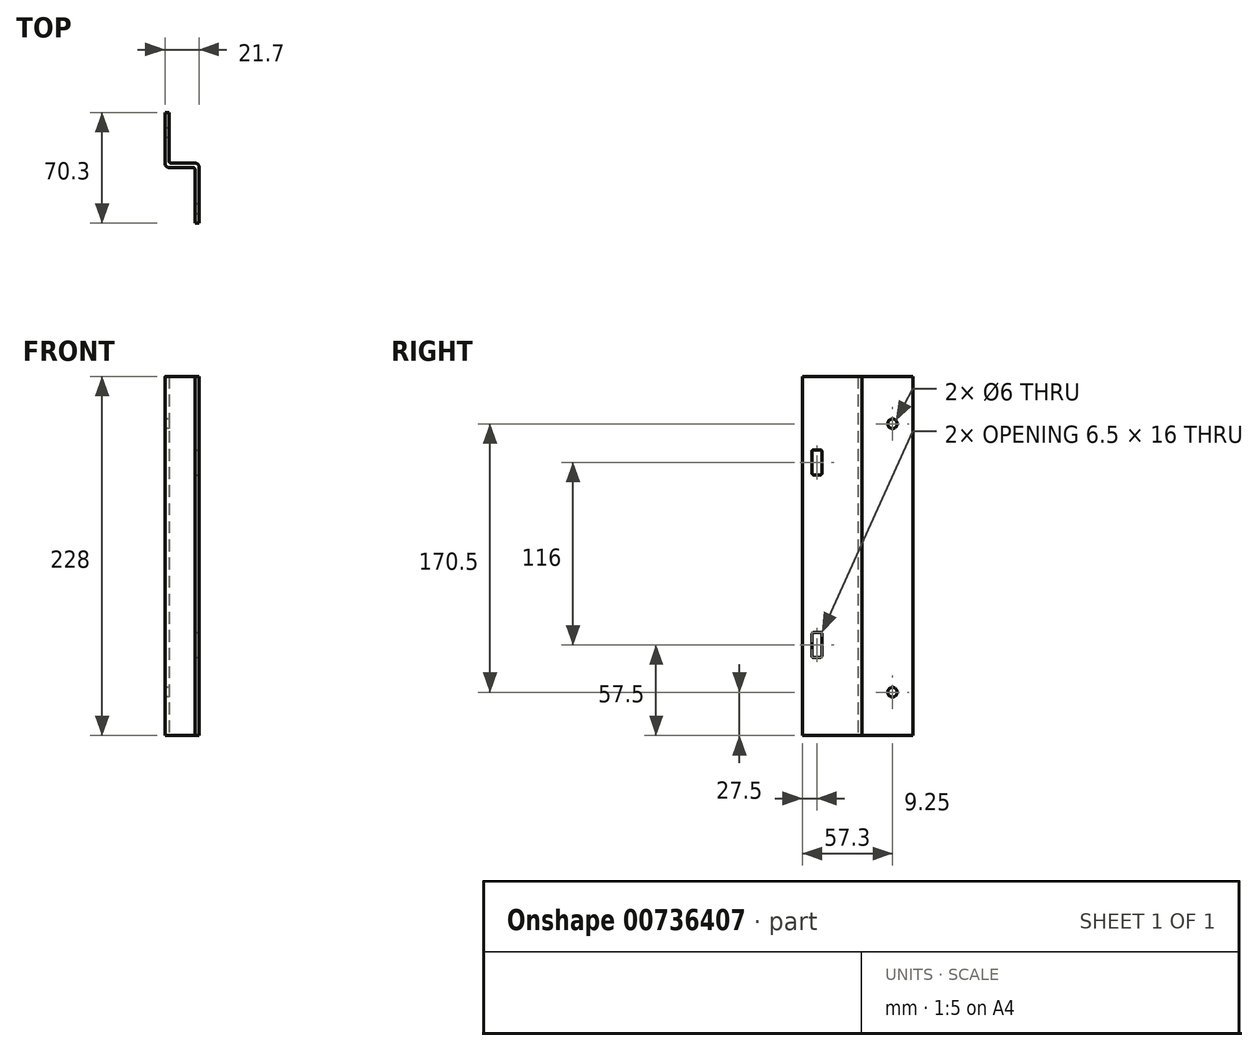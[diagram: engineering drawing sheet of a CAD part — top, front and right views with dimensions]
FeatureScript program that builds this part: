
annotation { "Feature Type Name" : "Feature", "Feature Type Description" : "" }
export const myFeature = defineFeature(function(context is Context, id is Id, definition is map)
    precondition{}
    {
        {
            var Q0;
            Q0=qCreatedBy(makeId("Top.planeOp"),FACE);
            var sketch = newSketch(context, id + "F0", { "sketchPlane" : qUnion([Q0])});
            skLineSegment(sketch, "E0", {"start": v(0, 0) * mm, "end": v(0, -32.5) * mm});
            skLineSegment(sketch, "E1", {"start": v(2.5, -35) * mm, "end": v(17.75, -35) * mm});
            skLineSegment(sketch, "E2", {"start": v(19, -36.25) * mm, "end": v(19, -70.3) * mm});
            skLineSegment(sketch, "E3", {"start": v(19, -70.3) * mm, "end": v(21.7, -70.3) * mm});
            skLineSegment(sketch, "E4", {"start": v(21.7, -70.3) * mm, "end": v(21.7, -34.8) * mm});
            skLineSegment(sketch, "E5", {"start": v(19.2, -32.3) * mm, "end": v(3.95, -32.3) * mm});
            skLineSegment(sketch, "E6", {"start": v(2.7, -31.05) * mm, "end": v(2.7, 0) * mm});
            skLineSegment(sketch, "E7", {"start": v(2.7, 0) * mm, "end": v(0, 0) * mm});
            skPoint(sketch, "E8.visualSharp", {"position": v(21.7, -32.3) * mm});
            skArc(sketch, "E8.filletArc", {"start": v(21.7, -34.8) * mm, "mid": v(20.97, -33.03) * mm, "end": v(19.2, -32.3) * mm});
            skPoint(sketch, "E9.visualSharp", {"position": v(0, -35) * mm});
            skArc(sketch, "E9.filletArc", {"start": v(0, -32.5) * mm, "mid": v(0.73, -34.27) * mm, "end": v(2.5, -35) * mm});
            skPoint(sketch, "E10.visualSharp", {"position": v(2.7, -32.3) * mm});
            skArc(sketch, "E10.filletArc", {"start": v(2.7, -31.05) * mm, "mid": v(3.07, -31.93) * mm, "end": v(3.95, -32.3) * mm});
            skPoint(sketch, "E11.visualSharp", {"position": v(19, -35) * mm});
            skArc(sketch, "E11.filletArc", {"start": v(19, -36.25) * mm, "mid": v(18.63, -35.37) * mm, "end": v(17.75, -35) * mm});
            skSolve(sketch);
        }
        {
            var Q0;
            Q0=makeQuery(id+"F0.imprint","IMPRINT",FACE,{"disambiguationData":[TD([[makeQuery(id+"F0.imprint","IMPRINT",EDGE,{"derivedFrom":sQuery(id+"F0.wireOp",EDGE,"E0")}),1.0]])]});
            extrude(context, id + "F1", {"entities" : qUnion([Q0]), "depth" : 228 * mm, "offsetDistance" : 25 * mm});
        }
        {
            var Q0;
            Q0=makeQuery(id+"F1.opExtrude","SWEPT_FACE",FACE,{"disambiguationData":[OSD([sQuery(id+"F0.wireOp",EDGE,"E0")])]});
            var sketch = newSketch(context, id + "F2", { "sketchPlane" : qUnion([Q0])});
            skCircle(sketch, "E12", {"center": v(13, 198) * mm, "radius": 3 * mm});
            skCircle(sketch, "E13", {"center": v(13, 27.5) * mm, "radius": 3 * mm});
            skSolve(sketch);
        }
        {
            var Q0;
            Q0=qSketchRegion(id+"F2",true);
            extrude(context, id + "F3", {"entities" : qUnion([Q0]), "operationType" : NewBodyOperationType.REMOVE, "oppositeDirection" : true, "depth" : 2.7 * mm, "offsetDistance" : 25 * mm});
        }
        {
            var Q0;
            Q0=makeQuery(id+"F1.opExtrude","SWEPT_FACE",FACE,{"disambiguationData":[OSD([sQuery(id+"F0.wireOp",EDGE,"E4")])]});
            var sketch = newSketch(context, id + "F4", { "sketchPlane" : qUnion([Q0])});
            skLineSegment(sketch, "E14.bottom", {"start": v(-59.05, 65.5) * mm, "end": v(-63.05, 65.5) * mm});
            skLineSegment(sketch, "E14.top", {"start": v(-59.05, 49.5) * mm, "end": v(-63.05, 49.5) * mm});
            skLineSegment(sketch, "E14.left", {"start": v(-57.8, 64.25) * mm, "end": v(-57.8, 50.75) * mm});
            skLineSegment(sketch, "E14.right", {"start": v(-64.3, 64.25) * mm, "end": v(-64.3, 50.75) * mm});
            skLineSegment(sketch, "E15.bottom", {"start": v(-59.05, 181.5) * mm, "end": v(-63.05, 181.5) * mm});
            skLineSegment(sketch, "E15.top", {"start": v(-59.05, 165.5) * mm, "end": v(-63.05, 165.5) * mm});
            skLineSegment(sketch, "E15.left", {"start": v(-57.8, 180.25) * mm, "end": v(-57.8, 166.75) * mm});
            skLineSegment(sketch, "E15.right", {"start": v(-64.3, 180.25) * mm, "end": v(-64.3, 166.75) * mm});
            skPoint(sketch, "E16.visualSharp", {"position": v(-57.8, 181.5) * mm});
            skArc(sketch, "E16.filletArc", {"start": v(-57.8, 180.25) * mm, "mid": v(-58.17, 181.13) * mm, "end": v(-59.05, 181.5) * mm});
            skPoint(sketch, "E17.visualSharp", {"position": v(-64.3, 181.5) * mm});
            skArc(sketch, "E17.filletArc", {"start": v(-63.05, 181.5) * mm, "mid": v(-63.93, 181.13) * mm, "end": v(-64.3, 180.25) * mm});
            skPoint(sketch, "E18.visualSharp", {"position": v(-57.8, 165.5) * mm});
            skArc(sketch, "E18.filletArc", {"start": v(-59.05, 165.5) * mm, "mid": v(-58.17, 165.87) * mm, "end": v(-57.8, 166.75) * mm});
            skPoint(sketch, "E19.visualSharp", {"position": v(-64.3, 165.5) * mm});
            skArc(sketch, "E19.filletArc", {"start": v(-64.3, 166.75) * mm, "mid": v(-63.93, 165.87) * mm, "end": v(-63.05, 165.5) * mm});
            skPoint(sketch, "E20.visualSharp", {"position": v(-57.8, 65.5) * mm});
            skArc(sketch, "E20.filletArc", {"start": v(-57.8, 64.25) * mm, "mid": v(-58.17, 65.13) * mm, "end": v(-59.05, 65.5) * mm});
            skPoint(sketch, "E21.visualSharp", {"position": v(-64.3, 65.5) * mm});
            skArc(sketch, "E21.filletArc", {"start": v(-63.05, 65.5) * mm, "mid": v(-63.93, 65.13) * mm, "end": v(-64.3, 64.25) * mm});
            skPoint(sketch, "E22.visualSharp", {"position": v(-64.3, 49.5) * mm});
            skArc(sketch, "E22.filletArc", {"start": v(-64.3, 50.75) * mm, "mid": v(-63.93, 49.87) * mm, "end": v(-63.05, 49.5) * mm});
            skPoint(sketch, "E23.visualSharp", {"position": v(-57.8, 49.5) * mm});
            skArc(sketch, "E23.filletArc", {"start": v(-59.05, 49.5) * mm, "mid": v(-58.17, 49.87) * mm, "end": v(-57.8, 50.75) * mm});
            skSolve(sketch);
        }
        {
            var Q0;
            Q0=qSketchRegion(id+"F4",true);
            extrude(context, id + "F5", {"entities" : qUnion([Q0]), "operationType" : NewBodyOperationType.REMOVE, "oppositeDirection" : true, "depth" : 2.7 * mm, "offsetDistance" : 25 * mm});
        }
    });
